SOLIDWORKS PART (.sldprt)
format: sldprt  version: not decoded by parser v0  size: 629,760 bytes
history: native  units: mm
features: sketch x18, cut_extrude x9, fillet x7, extrude x5, plane x4, pattern_linear x4, material x1, cut_revolve x1 (+13 scaffold rows collapsed)
feature tree (62):
  scaffold x13  (default folders/planes/origin — collapsed)
  material  "材质 <未指定>"
  plane  "前视基准面"
  plane  "上视基准面"
  plane  "右视基准面"
  sketch  "草图2"  dims[c1.D1=60.0mm c1.D2=25.0mm c2.D1=30.0mm c2.D2=85.0mm]
  extrude  "凸台-拉伸1"  Depth=1mm
  sketch  "草图3"  dims[c1.D2=37.5mm c1.D3=12.5mm c1.D4=1.0mm c1.D1=25.0mm c2.D2=2.5mm c2.D3=34.0mm c2.D1=1.0mm]
  cut_extrude  "切除-拉伸1"  Depth=1mm
  sketch  "草图5"  dims[D2=3.0mm D3=2.5mm D4=3.0mm D1=0.0mm]
  extrude  "凸台-拉伸2"  Depth=5mm
  fillet  "圆角1"  Radius=2mm
  sketch  "草图6"  dims[D1=0.0mm]
  cut_extrude  "切除-拉伸2"  Depth=4.5mm
  fillet  "圆角2"  Radius=0.2mm
  sketch  "草图7"  dims[D2=1.0mm D1=0.0mm]
  cut_extrude  "切除-拉伸3"  Depth=4.5mm
  pattern_linear  "阵列(线性)1"  Count1=5 Count2=1 Spacing1=5mm Spacing2=10mm
  sketch  "草图8"  dims[D1=2.5mm D2=2.5mm D3=20.0mm]
  plane  "基准面1"
  sketch  "草图9"  dims[c1.D4=0.75mm c1.D5=1.0mm c1.D7=2.0mm c1.D3=0.75mm c1.D6=1.5mm c2.D7=1.5mm c2.D4=1.5mm c2.D1=1.0mm c2.D2=3.0mm c2.D3=3.0mm c2.D6=1.5mm c3.D7=1.0mm c3.D1=1.5mm c3.D2=3.0mm c3.D4=5.0mm c3.D5=1.0mm]
  extrude  "凸台-拉伸3"  Depth=5mm
  sketch  "草图17"  dims[D1=0.1mm]
  cut_extrude  "切除-拉伸8"  Depth=5mm
  fillet  "圆角8"  Radius=0.05mm
  sketch  "草图18"  dims[D1=5.0mm D2=5.0mm D3=0.5mm D4=3.5mm D5=0.5mm D6=3.5mm]
  cut_revolve  "切除-旋转4"  Angle=360deg
  pattern_linear  "阵列(线性)3"  Count1=2 Count2=1 Spacing1=24mm Spacing2=10mm
  sketch  "草图19"  dims[D1=5.0mm D2=1.0mm D3=3.5mm]
  cut_extrude  "切除-拉伸9"  Depth=5mm
  fillet  "圆角9"  Radius=0.2mm
  sketch  "草图20"  dims[D1=4.0mm]
  cut_extrude  "切除-拉伸10"  Depth=2mm
  sketch  "草图21"  dims[D1=0.1mm D2=0.1mm D3=1.5mm]
  sketch  "草图23"  dims[D1=0.1mm D2=0.1mm D3=2.5mm]
  sketch  "草图24"  dims[D1=0.1mm]
  cut_extrude  "切除-拉伸11"  Depth=2.5mm
  pattern_linear  "阵列(线性)4"  Count1=2 Count2=1 Spacing1=50mm Spacing2=10mm
  sketch  "草图25"
  extrude  "凸台-拉伸4"  Depth=5mm
  sketch  "草图26"
  cut_extrude  "切除-拉伸12"  Depth=5mm
  fillet  "圆角11"  Radius=0.75mm
  fillet  "圆角12"  Radius=0.75mm
  sketch  "草图27"  dims[D1=0.5mm D2=0.5mm D3=1.0mm D4=1.0mm D5=10.0mm D6=10.0mm]
  extrude  "凸台-拉伸5"  Depth=1mm
  fillet  "圆角14"  Radius=0.3mm
  sketch  "草图28"  dims[D1=0.6mm]
  cut_extrude  "切除-拉伸13"  Depth=3mm
  pattern_linear  "阵列(线性)5"  Count1=2 Count2=1 Spacing1=50mm Spacing2=10mm
decode coverage: 42 of 44 modeling features carry decoded parameters
note: suppression state not decoded; provenance and decode notes live in map.json
